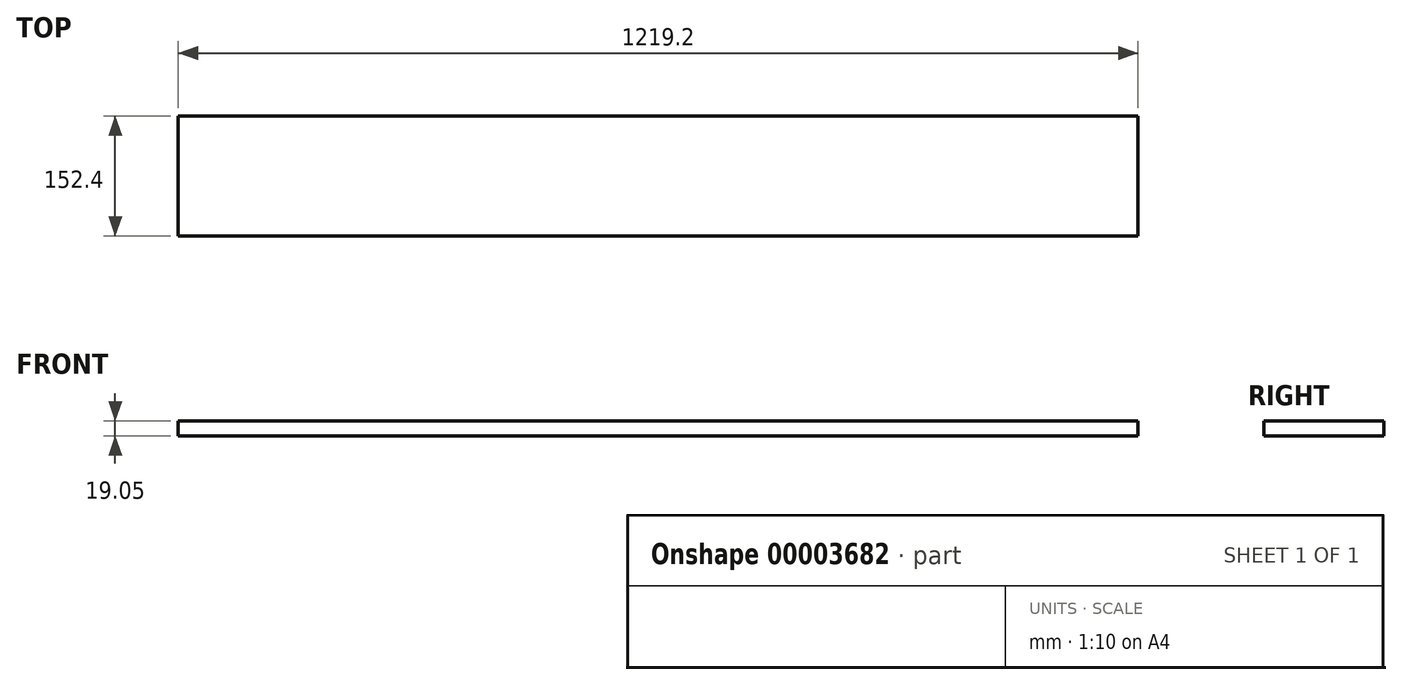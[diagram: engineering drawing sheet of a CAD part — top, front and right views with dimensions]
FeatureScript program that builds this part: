
annotation { "Feature Type Name" : "Feature", "Feature Type Description" : "" }
export const myFeature = defineFeature(function(context is Context, id is Id, definition is map)
    precondition{}
    {
        {
            var Q0;
            Q0=qCreatedBy(makeId("Top.planeOp"),FACE);
            var sketch = newSketch(context, id + "F0", { "sketchPlane" : qUnion([Q0])});
            skLineSegment(sketch, "E0.bottom", {"start": v(0, 0) * mm, "end": v(1219.2, 0) * mm});
            skLineSegment(sketch, "E0.top", {"start": v(0, -152.4) * mm, "end": v(1219.2, -152.4) * mm});
            skLineSegment(sketch, "E0.left", {"start": v(0, 0) * mm, "end": v(0, -152.4) * mm});
            skLineSegment(sketch, "E0.right", {"start": v(1219.2, 0) * mm, "end": v(1219.2, -152.4) * mm});
            skSolve(sketch);
        }
        {
            var Q0;
            Q0=makeQuery(id+"F0.imprint","IMPRINT",FACE,{"disambiguationData":[TD([[makeQuery(id+"F0.imprint","IMPRINT",EDGE,{"derivedFrom":sQuery(id+"F0.wireOp",EDGE,"E0.bottom")}),-1.0]])]});
            extrude(context, id + "F1", {"entities" : qUnion([Q0]), "depth" : 19.05 * mm});
        }
    });
